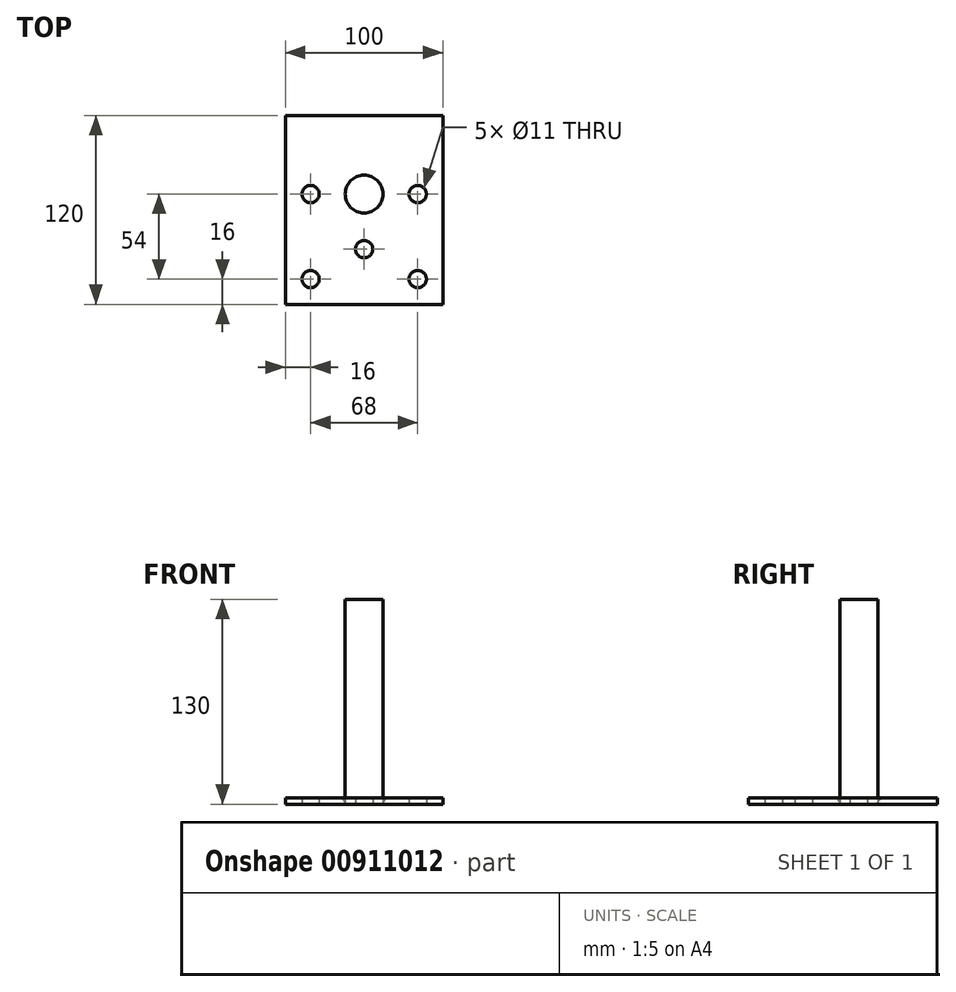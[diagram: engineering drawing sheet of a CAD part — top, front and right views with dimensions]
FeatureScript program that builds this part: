
annotation { "Feature Type Name" : "Feature", "Feature Type Description" : "" }
export const myFeature = defineFeature(function(context is Context, id is Id, definition is map)
    precondition{}
    {
        {
            var Q0;
            Q0=qCreatedBy(makeId("Top.planeOp"),FACE);
            var sketch = newSketch(context, id + "F0", { "sketchPlane" : qUnion([Q0])});
            skCircle(sketch, "E0", {"center": v(0, 0) * mm, "radius": 12 * mm});
            skLineSegment(sketch, "E1", {"start": v(0, 45.45) * mm, "end": v(0, -72.98) * mm, "construction": true});
            skLineSegment(sketch, "E2", {"start": v(0, 50) * mm, "end": v(50, 50) * mm});
            skLineSegment(sketch, "E3", {"start": v(50, 50) * mm, "end": v(50, -70) * mm});
            skLineSegment(sketch, "E4", {"start": v(50, -70) * mm, "end": v(0, -70) * mm});
            skLineSegment(sketch, "E5.MirrorCS", {"start": v(0, 50) * mm, "end": v(-50, 50) * mm});
            skLineSegment(sketch, "E6.MirrorCS", {"start": v(-50, 50) * mm, "end": v(-50, -70) * mm});
            skLineSegment(sketch, "E7.MirrorCS", {"start": v(-50, -70) * mm, "end": v(0, -70) * mm});
            skCircle(sketch, "E8", {"center": v(0, -35) * mm, "radius": 5.5 * mm});
            skCircle(sketch, "E9", {"center": v(34, 0) * mm, "radius": 5.5 * mm});
            skCircle(sketch, "E10", {"center": v(34, -54) * mm, "radius": 5.5 * mm});
            skCircle(sketch, "E11.MirrorC", {"center": v(-34, 0) * mm, "radius": 5.5 * mm});
            skCircle(sketch, "E12.MirrorC", {"center": v(-34, -54) * mm, "radius": 5.5 * mm});
            skSolve(sketch);
        }
        {
            var Q0;
            Q0=makeQuery(id+"F0.imprint","IMPRINT",FACE,{"disambiguationData":[TD([[makeQuery(id+"F0.imprint","IMPRINT",EDGE,{"derivedFrom":sQuery(id+"F0.wireOp",EDGE,"E0")}),-1.0]])]});
            extrude(context, id + "F1", {"entities" : qUnion([Q0]), "depth" : 4 * mm, "offsetDistance" : 25 * mm});
        }
        {
            var Q0;
            Q0=makeQuery(id+"F1.opExtrude","CAP_FACE",FACE,{"disambiguationData":[OSD([sQuery(id+"F0.wireOp",EDGE,"E0"),sQuery(id+"F0.wireOp",EDGE,"E2"),sQuery(id+"F0.wireOp",EDGE,"E3"),sQuery(id+"F0.wireOp",EDGE,"E4"),sQuery(id+"F0.wireOp",EDGE,"E5.MirrorCS"),sQuery(id+"F0.wireOp",EDGE,"E6.MirrorCS"),sQuery(id+"F0.wireOp",EDGE,"E7.MirrorCS"),sQuery(id+"F0.wireOp",EDGE,"E8"),sQuery(id+"F0.wireOp",EDGE,"E9"),sQuery(id+"F0.wireOp",EDGE,"E10"),sQuery(id+"F0.wireOp",EDGE,"E11.MirrorC"),sQuery(id+"F0.wireOp",EDGE,"E12.MirrorC")])],"isStart":true});
            var sketch = newSketch(context, id + "F2", { "sketchPlane" : qUnion([Q0])});
            skCircle(sketch, "E13", {"center": v(0, 0) * mm, "radius": 12 * mm});
            skSolve(sketch);
        }
        {
            var Q0;
            Q0 = qSketchRegion(id + "F2", true);
            extrude(context, id + "F3", {"entities" : qUnion([Q0]), "oppositeDirection" : true, "depth" : 130 * mm, "offsetDistance" : 25 * mm});
        }
        {
            var Q0;
            Q0=makeQuery(id+"F1.opExtrude","CAP_EDGE",EDGE,{"disambiguationData":[OSD([sQuery(id+"F0.wireOp",EDGE,"E0")])],"isStart":false});
            fillet(context, id + "F4", {"entities" : qUnion([Q0]), "radius" : 4 * mm, "tangentPropagation" : true, "allowEdgeOverflow" : false});
        }
    });
